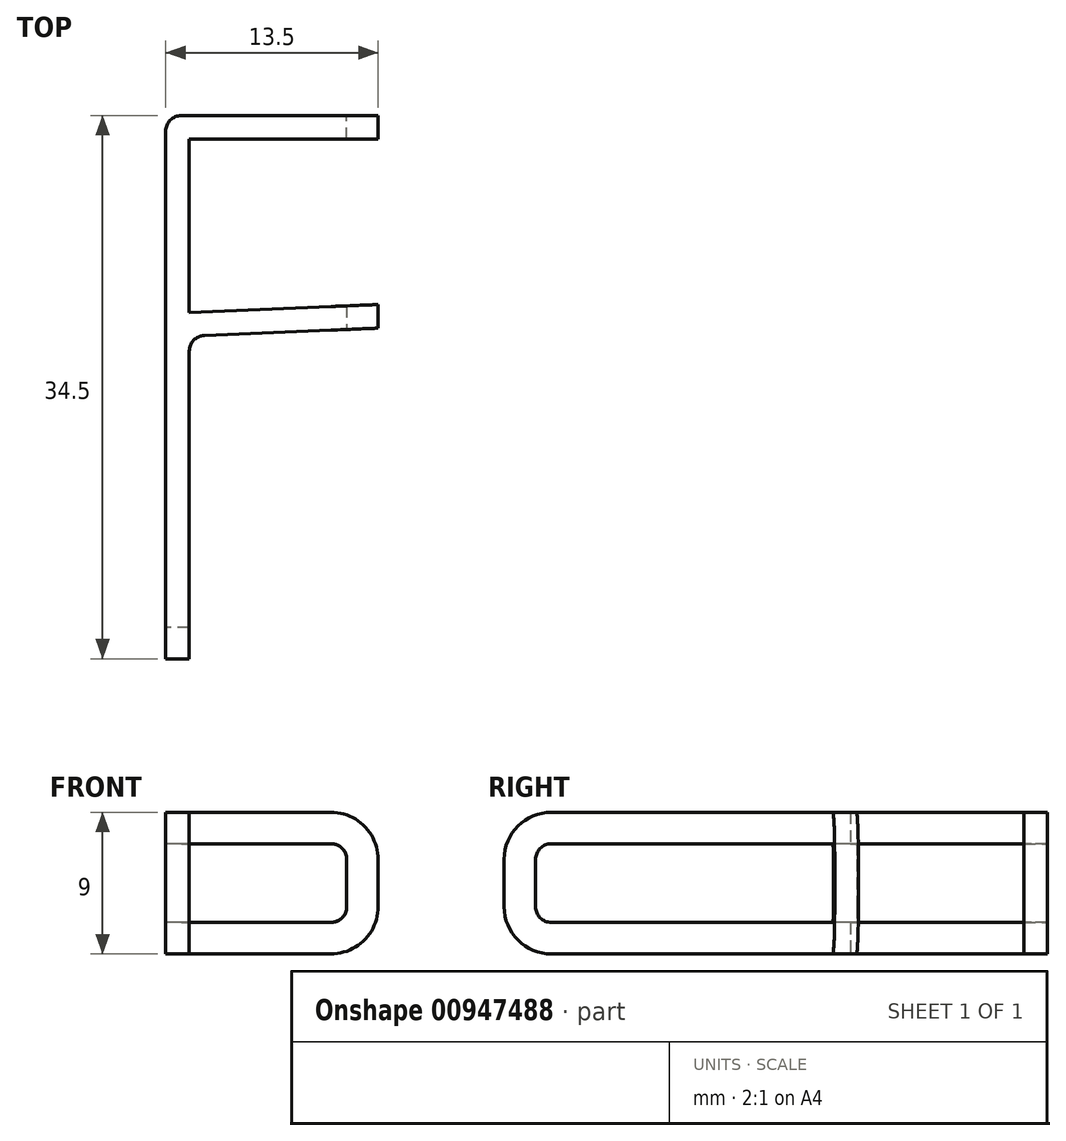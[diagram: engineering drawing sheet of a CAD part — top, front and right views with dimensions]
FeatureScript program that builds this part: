
annotation { "Feature Type Name" : "Feature", "Feature Type Description" : "" }
export const myFeature = defineFeature(function(context is Context, id is Id, definition is map)
    precondition{}
    {
        {
            var Q0;
            Q0=qCreatedBy(makeId("Top.planeOp"),FACE);
            var sketch = newSketch(context, id + "F0", { "sketchPlane" : qUnion([Q0])});
            skLineSegment(sketch, "E0", {"start": v(-63.6, 10) * mm, "end": v(-2.42, 20) * mm});
            skLineSegment(sketch, "E1", {"start": v(-2.42, 20) * mm, "end": v(-5.69, 40) * mm});
            skLineSegment(sketch, "E2", {"start": v(4.45, 40) * mm, "end": v(10.98, 0) * mm});
            skLineSegment(sketch, "E3", {"start": v(-0.76, 9.84) * mm, "end": v(0.85, 0) * mm});
            skLineSegment(sketch, "E4", {"start": v(0.85, 0) * mm, "end": v(10.98, 0) * mm});
            skLineSegment(sketch, "E5", {"start": v(-72.1, 0) * mm, "end": v(-63.6, 0) * mm});
            skLineSegment(sketch, "E6", {"start": v(-63.6, 0) * mm, "end": v(-0.76, 9.84) * mm});
            skLineSegment(sketch, "E7", {"start": v(-132.1, 0) * mm, "end": v(-120.08, 0) * mm});
            skLineSegment(sketch, "E8", {"start": v(-81.15, 53.94) * mm, "end": v(-72.1, 0) * mm});
            skLineSegment(sketch, "E9.trimOffspring", {"start": v(-71.34, 55.53) * mm, "end": v(-63.6, 10) * mm});
            skLineSegment(sketch, "E10", {"start": v(-73.25, 67.21) * mm, "end": v(-71.34, 55.53) * mm});
            skLineSegment(sketch, "E11", {"start": v(-87.24, 67.21) * mm, "end": v(-132.1, 0) * mm});
            skLineSegment(sketch, "E12.0", {"start": v(-81.74, 57.44) * mm, "end": v(-120.08, 0) * mm});
            skLineSegment(sketch, "E13", {"start": v(-72.1, 0) * mm, "end": v(-81.74, 57.44) * mm});
            skLineSegment(sketch, "E14", {"start": v(-87.24, 67.21) * mm, "end": v(-73.25, 67.21) * mm});
            skLineSegment(sketch, "E15", {"start": v(-2.42, 20) * mm, "end": v(2.58, 20) * mm});
            skLineSegment(sketch, "E16.0", {"start": v(-5.69, 40) * mm, "end": v(4.45, 40) * mm});
            skSolve(sketch);
        }
        {
            var Q0;
            Q0=makeQuery(id+"F0.imprint","IMPRINT",FACE,{"disambiguationData":[TD([[makeQuery(id+"F0.imprint","IMPRINT",EDGE,{"derivedFrom":sQuery(id+"F0.wireOp",EDGE,"E0")}),-1.0]])]});
            extrude(context, id + "F1", {"entities" : qUnion([Q0]), "depth" : 2.5 * mm, "offsetDistance" : 25 * mm, "hasSecondDirection" : true, "secondDirectionOppositeDirection" : true, "secondDirectionDepth" : 2.5 * mm});
        }
        {
            var Q0;
            Q0=makeQuery(id+"F1.opExtrude","CAP_EDGE",EDGE,{"disambiguationData":[OSD([sQuery(id+"F0.wireOp",EDGE,"E14")])],"isStart":false});
            chamfer(context, id + "F2", {"entities" : qUnion([Q0]), "chamferType" : ChamferType.TWO_OFFSETS, "width1" : 2 * mm, "oppositeDirection" : false, "width2" : 1 * mm, "tangentPropagation" : true});
        }
        {
            var Q0;
            {var subQ0=sQuery(id+"F0.wireOp",EDGE,"E14");Q0=makeQuery(id+"F2.opChamfer","BLEND_EDGE",EDGE,{"blendedFrom":[makeQuery(id+"F1.opExtrude","CAP_EDGE",EDGE,{"disambiguationData":[OSD([subQ0])],"isStart":false}),makeQuery(id+"F1.opExtrude","CAP_FACE",FACE,{"disambiguationData":[OSD([sQuery(id+"F0.wireOp",EDGE,"E0"),sQuery(id+"F0.wireOp",EDGE,"E1"),sQuery(id+"F0.wireOp",EDGE,"E2"),sQuery(id+"F0.wireOp",EDGE,"E3"),sQuery(id+"F0.wireOp",EDGE,"E4"),sQuery(id+"F0.wireOp",EDGE,"E5"),sQuery(id+"F0.wireOp",EDGE,"E6"),sQuery(id+"F0.wireOp",EDGE,"E7"),sQuery(id+"F0.wireOp",EDGE,"E9.trimOffspring"),sQuery(id+"F0.wireOp",EDGE,"E10"),sQuery(id+"F0.wireOp",EDGE,"E11"),sQuery(id+"F0.wireOp",EDGE,"E12.0"),sQuery(id+"F0.wireOp",EDGE,"E13"),subQ0,sQuery(id+"F0.wireOp",EDGE,"hnBKrzcR-41PN-ag7l-61eP-cGCsyuhvVwYe")])],"isStart":false})],"blendedInto":[makeQuery(id+"F1.opExtrude","CAP_FACE",FACE,{"disambiguationData":[OSD([sQuery(id+"F0.wireOp",EDGE,"E0"),sQuery(id+"F0.wireOp",EDGE,"E1"),sQuery(id+"F0.wireOp",EDGE,"E2"),sQuery(id+"F0.wireOp",EDGE,"E3"),sQuery(id+"F0.wireOp",EDGE,"E4"),sQuery(id+"F0.wireOp",EDGE,"E5"),sQuery(id+"F0.wireOp",EDGE,"E6"),sQuery(id+"F0.wireOp",EDGE,"E7"),sQuery(id+"F0.wireOp",EDGE,"E9.trimOffspring"),sQuery(id+"F0.wireOp",EDGE,"E10"),sQuery(id+"F0.wireOp",EDGE,"E11"),sQuery(id+"F0.wireOp",EDGE,"E12.0"),sQuery(id+"F0.wireOp",EDGE,"E13"),subQ0,sQuery(id+"F0.wireOp",EDGE,"hnBKrzcR-41PN-ag7l-61eP-cGCsyuhvVwYe")])],"isStart":false})]});}
            fillet(context, id + "F3", {"entities" : qUnion([Q0]), "radius" : 3 * mm, "tangentPropagation" : true, "allowEdgeOverflow" : false});
        }
        {
            var Q0;
            Q0=makeQuery(id+"F0.imprint","IMPRINT",FACE,{"disambiguationData":[TD([[makeQuery(id+"F0.imprint","IMPRINT",EDGE,{"derivedFrom":sQuery(id+"F0.wireOp",EDGE,"E0")}),-1.0]])]});
            extrude(context, id + "F4", {"entities" : qUnion([Q0]), "depth" : 9 * mm, "offsetDistance" : 25 * mm, "hasSecondDirection" : true, "secondDirectionOppositeDirection" : false, "secondDirectionDepth" : 4 * mm});
        }
        {
            var Q0;
            Q0=makeQuery(id+"F4.opExtrude","SWEPT_EDGE",EDGE,{"disambiguationData":[OSD([sQuery(id+"F0.wireOp",EDGE,"E12.0"),sQuery(id+"F0.wireOp",EDGE,"E13")])]});
            var Q1;
            Q1=makeQuery(id+"F1.opExtrude","SWEPT_EDGE",EDGE,{"disambiguationData":[OSD([sQuery(id+"F0.wireOp",EDGE,"E12.0"),sQuery(id+"F0.wireOp",EDGE,"E13")])]});
            var Q2;
            Q2=makeQuery(id+"F4.opExtrude","SWEPT_EDGE",EDGE,{"disambiguationData":[OSD([sQuery(id+"F0.wireOp",EDGE,"E5"),sQuery(id+"F0.wireOp",EDGE,"E13")])]});
            var Q3;
            Q3=makeQuery(id+"F1.opExtrude","SWEPT_EDGE",EDGE,{"disambiguationData":[OSD([sQuery(id+"F0.wireOp",EDGE,"E5"),sQuery(id+"F0.wireOp",EDGE,"E13")])]});
            var Q4;
            Q4=makeQuery(id+"F4.opExtrude","SWEPT_EDGE",EDGE,{"disambiguationData":[OSD([sQuery(id+"F0.wireOp",EDGE,"E7"),sQuery(id+"F0.wireOp",EDGE,"E12.0")])]});
            var Q5;
            Q5=makeQuery(id+"F1.opExtrude","SWEPT_EDGE",EDGE,{"disambiguationData":[OSD([sQuery(id+"F0.wireOp",EDGE,"E7"),sQuery(id+"F0.wireOp",EDGE,"E12.0")])]});
            var Q6;
            Q6=makeQuery(id+"F4.opExtrude","SWEPT_EDGE",EDGE,{"disambiguationData":[OSD([sQuery(id+"F0.wireOp",EDGE,"E3"),sQuery(id+"F0.wireOp",EDGE,"E4")])]});
            var Q7;
            Q7=makeQuery(id+"F1.opExtrude","SWEPT_EDGE",EDGE,{"disambiguationData":[OSD([sQuery(id+"F0.wireOp",EDGE,"E3"),sQuery(id+"F0.wireOp",EDGE,"E4")])]});
            var Q8;
            Q8=makeQuery(id+"F4.opExtrude","SWEPT_EDGE",EDGE,{"disambiguationData":[OSD([sQuery(id+"F0.wireOp",EDGE,"E11"),sQuery(id+"F0.wireOp",EDGE,"E14")])]});
            var Q9;
            Q9=makeQuery(id+"F1.opExtrude","SWEPT_EDGE",EDGE,{"disambiguationData":[OSD([sQuery(id+"F0.wireOp",EDGE,"E11"),sQuery(id+"F0.wireOp",EDGE,"E14")])]});
            var Q10;
            Q10=makeQuery(id+"F4.opExtrude","SWEPT_EDGE",EDGE,{"disambiguationData":[OSD([sQuery(id+"F0.wireOp",EDGE,"E10"),sQuery(id+"F0.wireOp",EDGE,"E14")])]});
            var Q11;
            Q11=makeQuery(id+"F1.opExtrude","SWEPT_EDGE",EDGE,{"disambiguationData":[OSD([sQuery(id+"F0.wireOp",EDGE,"E10"),sQuery(id+"F0.wireOp",EDGE,"E14")])]});
            var Q12;
            Q12=makeQuery(id+"F4.opExtrude","SWEPT_EDGE",EDGE,{"disambiguationData":[OSD([sQuery(id+"F0.wireOp",EDGE,"E2"),sQuery(id+"F0.wireOp",EDGE,"E16.0")])]});
            var Q13;
            Q13=makeQuery(id+"F1.opExtrude","SWEPT_EDGE",EDGE,{"disambiguationData":[OSD([sQuery(id+"F0.wireOp",EDGE,"E2"),sQuery(id+"F0.wireOp",EDGE,"E16.0")])]});
            fillet(context, id + "F5", {"entities" : qUnion([Q0, Q1, Q2, Q3, Q4, Q5, Q6, Q7, Q8, Q9, Q10, Q11, Q12, Q13]), "radius" : 5 * mm, "tangentPropagation" : true, "allowEdgeOverflow" : false});
        }
        {
            var Q0;
            Q0=makeQuery(id+"F1.opExtrude","SWEPT_EDGE",EDGE,{"disambiguationData":[OSD([sQuery(id+"F0.wireOp",EDGE,"E0"),sQuery(id+"F0.wireOp",EDGE,"E1")])]});
            var Q1;
            Q1=makeQuery(id+"F4.opExtrude","SWEPT_EDGE",EDGE,{"disambiguationData":[OSD([sQuery(id+"F0.wireOp",EDGE,"E0"),sQuery(id+"F0.wireOp",EDGE,"E1")])]});
            var Q2;
            Q2=makeQuery(id+"F4.opExtrude","SWEPT_EDGE",EDGE,{"disambiguationData":[OSD([sQuery(id+"F0.wireOp",EDGE,"E0"),sQuery(id+"F0.wireOp",EDGE,"E9.trimOffspring")])]});
            var Q3;
            Q3=makeQuery(id+"F1.opExtrude","SWEPT_EDGE",EDGE,{"disambiguationData":[OSD([sQuery(id+"F0.wireOp",EDGE,"E0"),sQuery(id+"F0.wireOp",EDGE,"E9.trimOffspring")])]});
            var Q4;
            Q4=makeQuery(id+"F1.opExtrude","SWEPT_EDGE",EDGE,{"disambiguationData":[OSD([sQuery(id+"F0.wireOp",EDGE,"E3"),sQuery(id+"F0.wireOp",EDGE,"E6")])]});
            var Q5;
            Q5=makeQuery(id+"F4.opExtrude","SWEPT_EDGE",EDGE,{"disambiguationData":[OSD([sQuery(id+"F0.wireOp",EDGE,"E3"),sQuery(id+"F0.wireOp",EDGE,"E6")])]});
            var Q6;
            Q6=makeQuery(id+"F1.opExtrude","SWEPT_EDGE",EDGE,{"disambiguationData":[OSD([sQuery(id+"F0.wireOp",EDGE,"E1"),sQuery(id+"F0.wireOp",EDGE,"hnBKrzcR-41PN-ag7l-61eP-cGCsyuhvVwYe")])]});
            var Q7;
            Q7=makeQuery(id+"F4.opExtrude","SWEPT_EDGE",EDGE,{"disambiguationData":[OSD([sQuery(id+"F0.wireOp",EDGE,"E1"),sQuery(id+"F0.wireOp",EDGE,"hnBKrzcR-41PN-ag7l-61eP-cGCsyuhvVwYe")])]});
            var Q8;
            Q8=makeQuery(id+"F4.opExtrude","SWEPT_EDGE",EDGE,{"disambiguationData":[OSD([sQuery(id+"F0.wireOp",EDGE,"E2"),sQuery(id+"F0.wireOp",EDGE,"E4")])]});
            var Q9;
            Q9=makeQuery(id+"F1.opExtrude","SWEPT_EDGE",EDGE,{"disambiguationData":[OSD([sQuery(id+"F0.wireOp",EDGE,"E2"),sQuery(id+"F0.wireOp",EDGE,"E4")])]});
            var Q10;
            Q10=makeQuery(id+"F1.opExtrude","SWEPT_EDGE",EDGE,{"disambiguationData":[OSD([sQuery(id+"F0.wireOp",EDGE,"E7"),sQuery(id+"F0.wireOp",EDGE,"E11")])]});
            var Q11;
            Q11=makeQuery(id+"F4.opExtrude","SWEPT_EDGE",EDGE,{"disambiguationData":[OSD([sQuery(id+"F0.wireOp",EDGE,"E7"),sQuery(id+"F0.wireOp",EDGE,"E11")])]});
            fillet(context, id + "F6", {"entities" : qUnion([Q0, Q1, Q2, Q3, Q4, Q5, Q6, Q7, Q8, Q9, Q10, Q11]), "radius" : 2 * mm, "tangentPropagation" : true, "allowEdgeOverflow" : false});
        }
        {
            var Q0;
            Q0=qCreatedBy(makeId("Top.planeOp"),FACE);
            var sketch = newSketch(context, id + "F7", { "sketchPlane" : qUnion([Q0])});
            skLineSegment(sketch, "E17", {"start": v(-79.91, 59.99) * mm, "end": v(-79.91, 60.49) * mm});
            skLineSegment(sketch, "E18", {"start": v(-79.91, 60.49) * mm, "end": v(-79.91, 65.49) * mm});
            skLineSegment(sketch, "E19", {"start": v(-79.91, 65.49) * mm, "end": v(-82.41, 65.49) * mm});
            skLineSegment(sketch, "E20", {"start": v(-79.91, 65.49) * mm, "end": v(-77.41, 65.49) * mm});
            skLineSegment(sketch, "E21", {"start": v(-77.41, 65.49) * mm, "end": v(-77.41, 60.49) * mm});
            skLineSegment(sketch, "E22", {"start": v(-77.41, 60.49) * mm, "end": v(-79.91, 60.49) * mm});
            skLineSegment(sketch, "E23", {"start": v(-79.91, 60.49) * mm, "end": v(-82.41, 60.49) * mm});
            skLineSegment(sketch, "E24", {"start": v(-82.41, 60.49) * mm, "end": v(-82.41, 65.49) * mm});
            skLineSegment(sketch, "E25.0", {"start": v(-79.91, 65.99) * mm, "end": v(-76.91, 65.99) * mm});
            skLineSegment(sketch, "E25.1", {"start": v(-82.91, 59.99) * mm, "end": v(-82.91, 65.99) * mm});
            skLineSegment(sketch, "E25.2", {"start": v(-79.91, 59.99) * mm, "end": v(-82.91, 59.99) * mm});
            skLineSegment(sketch, "E25.3", {"start": v(-79.91, 65.99) * mm, "end": v(-82.91, 65.99) * mm});
            skLineSegment(sketch, "E25.4", {"start": v(-76.91, 59.99) * mm, "end": v(-79.91, 59.99) * mm});
            skLineSegment(sketch, "E25.5", {"start": v(-76.91, 65.99) * mm, "end": v(-76.91, 59.99) * mm});
            skLineSegment(sketch, "E26", {"start": v(-82.41, 62.99) * mm, "end": v(-85.71, 62.99) * mm});
            skLineSegment(sketch, "E27", {"start": v(-85.71, 62.99) * mm, "end": v(-85.71, 63.49) * mm});
            skLineSegment(sketch, "E28", {"start": v(-85.71, 63.49) * mm, "end": v(-82.41, 65.49) * mm});
            skLineSegment(sketch, "E29.0", {"start": v(-86.21, 62.99) * mm, "end": v(-86.21, 63.49) * mm});
            skLineSegment(sketch, "E30", {"start": v(-86.21, 63.49) * mm, "end": v(-82.09, 65.99) * mm});
            skLineSegment(sketch, "E31", {"start": v(-86.21, 62.99) * mm, "end": v(-85.71, 62.99) * mm});
            skLineSegment(sketch, "E32", {"start": v(-82.41, 62.99) * mm, "end": v(-77.41, 62.99) * mm});
            skLineSegment(sketch, "E33.MirrorCS", {"start": v(-73.61, 63.49) * mm, "end": v(-77.74, 65.99) * mm});
            skLineSegment(sketch, "E34.MirrorCS", {"start": v(-74.11, 63.49) * mm, "end": v(-77.41, 65.49) * mm});
            skLineSegment(sketch, "E35.MirrorCS", {"start": v(-73.61, 62.99) * mm, "end": v(-73.61, 63.49) * mm});
            skLineSegment(sketch, "E36.MirrorCS", {"start": v(-74.11, 62.99) * mm, "end": v(-74.11, 63.49) * mm});
            skLineSegment(sketch, "E37.MirrorCS", {"start": v(-73.61, 62.99) * mm, "end": v(-74.11, 62.99) * mm});
            skLineSegment(sketch, "E38.MirrorCS", {"start": v(-77.41, 62.99) * mm, "end": v(-74.11, 62.99) * mm});
            skLineSegment(sketch, "E39", {"start": v(-82.91, 65.99) * mm, "end": v(-82.91, 68.99) * mm});
            skLineSegment(sketch, "E40", {"start": v(-82.91, 68.99) * mm, "end": v(-76.91, 68.99) * mm});
            skLineSegment(sketch, "E41", {"start": v(-76.91, 68.99) * mm, "end": v(-76.91, 65.99) * mm});
            skSolve(sketch);
        }
        {
            var Q0;
            {var subQ0=sQuery(id+"F7.wireOp",EDGE,"E39");Q0=makeQuery(id+"F7.imprint","IMPRINT",FACE,{"disambiguationData":[TD([[makeQuery(id+"F7.imprint","IMPRINT",EDGE,{"derivedFrom":subQ0}),-1.0]])]});}
            var Q1;
            {var subQ15=sQuery(id+"F7.wireOp",EDGE,"E19");Q1=makeQuery(id+"F7.imprint","IMPRINT",FACE,{"disambiguationData":[TD([[makeQuery(id+"F7.imprint","IMPRINT",EDGE,{"derivedFrom":subQ15}),-1.0]])]});}
            var Q2;
            {var subQ0=sQuery(id+"F7.wireOp",EDGE,"E25.3");var subQ3=sQuery(id+"F7.wireOp",EDGE,"E30");var subQ5=makeQuery(id+"F7.imprint","INTERSECT",VERTEX,{"derivedFrom":[subQ0,subQ3]});Q2=makeQuery(id+"F7.imprint","IMPRINT",FACE,{"disambiguationData":[TD([[makeQuery(id+"F7.imprint","IMPRINT",EDGE,{"disambiguationData":[TD([[subQ5,1.0]])],"derivedFrom":subQ3}),1.0]])]});}
            var Q3;
            {var subQ1=sQuery(id+"F7.wireOp",EDGE,"E25.0");var subQ3=sQuery(id+"F7.wireOp",EDGE,"E33.MirrorCS");var subQ4=makeQuery(id+"F7.imprint","INTERSECT",VERTEX,{"derivedFrom":[subQ1,subQ3]});Q3=makeQuery(id+"F7.imprint","IMPRINT",FACE,{"disambiguationData":[TD([[makeQuery(id+"F7.imprint","IMPRINT",EDGE,{"disambiguationData":[TD([[subQ4,1.0]])],"derivedFrom":subQ3}),-1.0]])]});}
            var Q4;
            {var subQ3=sQuery(id+"F7.wireOp",EDGE,"E26");var subQ5=sQuery(id+"F7.wireOp",EDGE,"E25.1");var subQ6=makeQuery(id+"F7.imprint","INTERSECT",VERTEX,{"derivedFrom":[subQ5,subQ3]});Q4=makeQuery(id+"F7.imprint","IMPRINT",FACE,{"disambiguationData":[TD([[makeQuery(id+"F7.imprint","IMPRINT",EDGE,{"disambiguationData":[TD([[subQ6,-1.0]])],"derivedFrom":subQ5}),-1.0]])]});}
            var Q5;
            {var subQ0=sQuery(id+"F7.wireOp",EDGE,"E19");Q5=makeQuery(id+"F7.imprint","IMPRINT",FACE,{"disambiguationData":[TD([[makeQuery(id+"F7.imprint","IMPRINT",EDGE,{"derivedFrom":subQ0}),1.0]])]});}
            var Q6;
            {var subQ0=sQuery(id+"F7.wireOp",EDGE,"E20");Q6=makeQuery(id+"F7.imprint","IMPRINT",FACE,{"disambiguationData":[TD([[makeQuery(id+"F7.imprint","IMPRINT",EDGE,{"derivedFrom":subQ0}),-1.0]])]});}
            var Q7;
            {var subQ3=sQuery(id+"F7.wireOp",EDGE,"E38.MirrorCS");var subQ5=sQuery(id+"F7.wireOp",EDGE,"E25.5");var subQ6=makeQuery(id+"F7.imprint","INTERSECT",VERTEX,{"derivedFrom":[subQ5,subQ3]});Q7=makeQuery(id+"F7.imprint","IMPRINT",FACE,{"disambiguationData":[TD([[makeQuery(id+"F7.imprint","IMPRINT",EDGE,{"disambiguationData":[TD([[subQ6,1.0]])],"derivedFrom":subQ5}),-1.0]])]});}
            var Q8;
            Q8=sQuery(id+"F7.wireOp",EDGE,"E32");
            revolve(context, id + "F8", {"operationType" : NewBodyOperationType.REMOVE, "surfaceOperationType" : NewSurfaceOperationType.NEW, "entities" : qUnion([Q0, Q1, Q2, Q3, Q4, Q5, Q6, Q7]), "axis" : qUnion([Q8]), "revolveType" : RevolveType.ONE_DIRECTION, "oppositeDirection" : true, "angle" : 90 * degree});
        }
        {
            var Q0;
            {var subQ0=sQuery(id+"F7.wireOp",EDGE,"E39");Q0=makeQuery(id+"F7.imprint","IMPRINT",FACE,{"disambiguationData":[TD([[makeQuery(id+"F7.imprint","IMPRINT",EDGE,{"derivedFrom":subQ0}),-1.0]])]});}
            var Q1;
            {var subQ0=sQuery(id+"F7.wireOp",EDGE,"E25.3");var subQ3=sQuery(id+"F7.wireOp",EDGE,"E30");var subQ5=makeQuery(id+"F7.imprint","INTERSECT",VERTEX,{"derivedFrom":[subQ0,subQ3]});Q1=makeQuery(id+"F7.imprint","IMPRINT",FACE,{"disambiguationData":[TD([[makeQuery(id+"F7.imprint","IMPRINT",EDGE,{"disambiguationData":[TD([[subQ5,1.0]])],"derivedFrom":subQ3}),1.0]])]});}
            var Q2;
            {var subQ1=sQuery(id+"F7.wireOp",EDGE,"E25.0");var subQ3=sQuery(id+"F7.wireOp",EDGE,"E33.MirrorCS");var subQ4=makeQuery(id+"F7.imprint","INTERSECT",VERTEX,{"derivedFrom":[subQ1,subQ3]});Q2=makeQuery(id+"F7.imprint","IMPRINT",FACE,{"disambiguationData":[TD([[makeQuery(id+"F7.imprint","IMPRINT",EDGE,{"disambiguationData":[TD([[subQ4,1.0]])],"derivedFrom":subQ3}),-1.0]])]});}
            var Q3;
            {var subQ15=sQuery(id+"F7.wireOp",EDGE,"E19");Q3=makeQuery(id+"F7.imprint","IMPRINT",FACE,{"disambiguationData":[TD([[makeQuery(id+"F7.imprint","IMPRINT",EDGE,{"derivedFrom":subQ15}),-1.0]])]});}
            var Q4;
            {var subQ3=sQuery(id+"F7.wireOp",EDGE,"E26");var subQ5=sQuery(id+"F7.wireOp",EDGE,"E25.1");var subQ6=makeQuery(id+"F7.imprint","INTERSECT",VERTEX,{"derivedFrom":[subQ5,subQ3]});Q4=makeQuery(id+"F7.imprint","IMPRINT",FACE,{"disambiguationData":[TD([[makeQuery(id+"F7.imprint","IMPRINT",EDGE,{"disambiguationData":[TD([[subQ6,-1.0]])],"derivedFrom":subQ5}),-1.0]])]});}
            var Q5;
            {var subQ0=sQuery(id+"F7.wireOp",EDGE,"E19");Q5=makeQuery(id+"F7.imprint","IMPRINT",FACE,{"disambiguationData":[TD([[makeQuery(id+"F7.imprint","IMPRINT",EDGE,{"derivedFrom":subQ0}),1.0]])]});}
            var Q6;
            {var subQ0=sQuery(id+"F7.wireOp",EDGE,"E20");Q6=makeQuery(id+"F7.imprint","IMPRINT",FACE,{"disambiguationData":[TD([[makeQuery(id+"F7.imprint","IMPRINT",EDGE,{"derivedFrom":subQ0}),-1.0]])]});}
            var Q7;
            {var subQ3=sQuery(id+"F7.wireOp",EDGE,"E38.MirrorCS");var subQ5=sQuery(id+"F7.wireOp",EDGE,"E25.5");var subQ6=makeQuery(id+"F7.imprint","INTERSECT",VERTEX,{"derivedFrom":[subQ5,subQ3]});Q7=makeQuery(id+"F7.imprint","IMPRINT",FACE,{"disambiguationData":[TD([[makeQuery(id+"F7.imprint","IMPRINT",EDGE,{"disambiguationData":[TD([[subQ6,1.0]])],"derivedFrom":subQ5}),-1.0]])]});}
            var Q8;
            Q8=makeQuery(id+"F7.imprint","IMPRINT",FACE,{"disambiguationData":[TD([[makeQuery(id+"F7.imprint","IMPRINT",EDGE,{"derivedFrom":sQuery(id+"F7.wireOp",EDGE,"E17")}),1.0]])]});
            var Q9;
            {var subQ0=sQuery(id+"F7.wireOp",EDGE,"E23");Q9=makeQuery(id+"F7.imprint","IMPRINT",FACE,{"disambiguationData":[TD([[makeQuery(id+"F7.imprint","IMPRINT",EDGE,{"derivedFrom":subQ0}),-1.0]])]});}
            var Q10;
            {var subQ0=sQuery(id+"F7.wireOp",EDGE,"E22");Q10=makeQuery(id+"F7.imprint","IMPRINT",FACE,{"disambiguationData":[TD([[makeQuery(id+"F7.imprint","IMPRINT",EDGE,{"derivedFrom":subQ0}),-1.0]])]});}
            var Q11;
            Q11=makeQuery(id+"F7.imprint","IMPRINT",FACE,{"disambiguationData":[TD([[makeQuery(id+"F7.imprint","IMPRINT",EDGE,{"derivedFrom":sQuery(id+"F7.wireOp",EDGE,"E17")}),-1.0]])]});
            extrude(context, id + "F9", {"entities" : qUnion([Q0, Q1, Q2, Q3, Q4, Q5, Q6, Q7, Q8, Q9, Q10, Q11]), "operationType" : NewBodyOperationType.REMOVE, "depth" : 10 * mm, "offsetDistance" : 25 * mm});
        }
        {
            var Q0;
            {var subQ1=sQuery(id+"F7.wireOp",EDGE,"E27");Q0=makeQuery(id+"F7.imprint","IMPRINT",FACE,{"disambiguationData":[TD([[makeQuery(id+"F7.imprint","IMPRINT",EDGE,{"derivedFrom":subQ1}),1.0]])]});}
            var Q1;
            {var subQ5=sQuery(id+"F7.wireOp",EDGE,"E27");Q1=makeQuery(id+"F7.imprint","IMPRINT",FACE,{"disambiguationData":[TD([[makeQuery(id+"F7.imprint","IMPRINT",EDGE,{"derivedFrom":subQ5}),-1.0]])]});}
            var Q2;
            {var subQ15=sQuery(id+"F7.wireOp",EDGE,"E19");Q2=makeQuery(id+"F7.imprint","IMPRINT",FACE,{"disambiguationData":[TD([[makeQuery(id+"F7.imprint","IMPRINT",EDGE,{"derivedFrom":subQ15}),-1.0]])]});}
            var Q3;
            {var subQ3=sQuery(id+"F7.wireOp",EDGE,"E26");var subQ5=sQuery(id+"F7.wireOp",EDGE,"E25.1");var subQ6=makeQuery(id+"F7.imprint","INTERSECT",VERTEX,{"derivedFrom":[subQ5,subQ3]});Q3=makeQuery(id+"F7.imprint","IMPRINT",FACE,{"disambiguationData":[TD([[makeQuery(id+"F7.imprint","IMPRINT",EDGE,{"disambiguationData":[TD([[subQ6,-1.0]])],"derivedFrom":subQ5}),-1.0]])]});}
            var Q4;
            {var subQ0=sQuery(id+"F7.wireOp",EDGE,"E19");Q4=makeQuery(id+"F7.imprint","IMPRINT",FACE,{"disambiguationData":[TD([[makeQuery(id+"F7.imprint","IMPRINT",EDGE,{"derivedFrom":subQ0}),1.0]])]});}
            var Q5;
            {var subQ0=sQuery(id+"F7.wireOp",EDGE,"E20");Q5=makeQuery(id+"F7.imprint","IMPRINT",FACE,{"disambiguationData":[TD([[makeQuery(id+"F7.imprint","IMPRINT",EDGE,{"derivedFrom":subQ0}),-1.0]])]});}
            var Q6;
            {var subQ3=sQuery(id+"F7.wireOp",EDGE,"E38.MirrorCS");var subQ5=sQuery(id+"F7.wireOp",EDGE,"E25.5");var subQ6=makeQuery(id+"F7.imprint","INTERSECT",VERTEX,{"derivedFrom":[subQ5,subQ3]});Q6=makeQuery(id+"F7.imprint","IMPRINT",FACE,{"disambiguationData":[TD([[makeQuery(id+"F7.imprint","IMPRINT",EDGE,{"disambiguationData":[TD([[subQ6,1.0]])],"derivedFrom":subQ5}),-1.0]])]});}
            var Q7;
            {var subQ5=sQuery(id+"F7.wireOp",EDGE,"E36.MirrorCS");Q7=makeQuery(id+"F7.imprint","IMPRINT",FACE,{"disambiguationData":[TD([[makeQuery(id+"F7.imprint","IMPRINT",EDGE,{"derivedFrom":subQ5}),1.0]])]});}
            var Q8;
            {var subQ0=sQuery(id+"F7.wireOp",EDGE,"E35.MirrorCS");Q8=makeQuery(id+"F7.imprint","IMPRINT",FACE,{"disambiguationData":[TD([[makeQuery(id+"F7.imprint","IMPRINT",EDGE,{"derivedFrom":subQ0}),1.0]])]});}
            var Q9;
            Q9=sQuery(id+"F7.wireOp",EDGE,"E38.MirrorCS");
            revolve(context, id + "F10", {"operationType" : NewBodyOperationType.REMOVE, "surfaceOperationType" : NewSurfaceOperationType.NEW, "entities" : qUnion([Q0, Q1, Q2, Q3, Q4, Q5, Q6, Q7, Q8]), "axis" : qUnion([Q9]), "revolveType" : RevolveType.FULL});
        }
        {
            var Q0;
            {var subQ0=sQuery(id+"F7.wireOp",EDGE,"E20");Q0=makeQuery(id+"F7.imprint","IMPRINT",FACE,{"disambiguationData":[TD([[makeQuery(id+"F7.imprint","IMPRINT",EDGE,{"derivedFrom":subQ0}),-1.0]])]});}
            var Q1;
            {var subQ0=sQuery(id+"F7.wireOp",EDGE,"E19");Q1=makeQuery(id+"F7.imprint","IMPRINT",FACE,{"disambiguationData":[TD([[makeQuery(id+"F7.imprint","IMPRINT",EDGE,{"derivedFrom":subQ0}),1.0]])]});}
            var Q2;
            {var subQ0=sQuery(id+"F7.wireOp",EDGE,"E22");Q2=makeQuery(id+"F7.imprint","IMPRINT",FACE,{"disambiguationData":[TD([[makeQuery(id+"F7.imprint","IMPRINT",EDGE,{"derivedFrom":subQ0}),-1.0]])]});}
            var Q3;
            {var subQ0=sQuery(id+"F7.wireOp",EDGE,"E23");Q3=makeQuery(id+"F7.imprint","IMPRINT",FACE,{"disambiguationData":[TD([[makeQuery(id+"F7.imprint","IMPRINT",EDGE,{"derivedFrom":subQ0}),-1.0]])]});}
            extrude(context, id + "F11", {"entities" : qUnion([Q0, Q1, Q2, Q3]), "operationType" : NewBodyOperationType.REMOVE, "depth" : 8 * mm, "offsetDistance" : 25 * mm});
        }
        {
            var Q0;
            {var subQ0=sQuery(id+"F7.wireOp",EDGE,"E19");Q0=makeQuery(id+"F7.imprint","IMPRINT",FACE,{"disambiguationData":[TD([[makeQuery(id+"F7.imprint","IMPRINT",EDGE,{"derivedFrom":subQ0}),1.0]])]});}
            var Q1;
            {var subQ0=sQuery(id+"F7.wireOp",EDGE,"E20");Q1=makeQuery(id+"F7.imprint","IMPRINT",FACE,{"disambiguationData":[TD([[makeQuery(id+"F7.imprint","IMPRINT",EDGE,{"derivedFrom":subQ0}),-1.0]])]});}
            var Q2;
            {var subQ0=sQuery(id+"F7.wireOp",EDGE,"E23");Q2=makeQuery(id+"F7.imprint","IMPRINT",FACE,{"disambiguationData":[TD([[makeQuery(id+"F7.imprint","IMPRINT",EDGE,{"derivedFrom":subQ0}),-1.0]])]});}
            var Q3;
            {var subQ0=sQuery(id+"F7.wireOp",EDGE,"E22");Q3=makeQuery(id+"F7.imprint","IMPRINT",FACE,{"disambiguationData":[TD([[makeQuery(id+"F7.imprint","IMPRINT",EDGE,{"derivedFrom":subQ0}),-1.0]])]});}
            extrude(context, id + "F12", {"entities" : qUnion([Q0, Q1, Q2, Q3]), "depth" : 8 * mm, "offsetDistance" : 25 * mm});
        }
        {
            var Q0;
            {var subQ5=sQuery(id+"F7.wireOp",EDGE,"E27");Q0=makeQuery(id+"F7.imprint","IMPRINT",FACE,{"disambiguationData":[TD([[makeQuery(id+"F7.imprint","IMPRINT",EDGE,{"derivedFrom":subQ5}),-1.0]])]});}
            var Q1;
            {var subQ3=sQuery(id+"F7.wireOp",EDGE,"E26");var subQ5=sQuery(id+"F7.wireOp",EDGE,"E25.1");var subQ6=makeQuery(id+"F7.imprint","INTERSECT",VERTEX,{"derivedFrom":[subQ5,subQ3]});Q1=makeQuery(id+"F7.imprint","IMPRINT",FACE,{"disambiguationData":[TD([[makeQuery(id+"F7.imprint","IMPRINT",EDGE,{"disambiguationData":[TD([[subQ6,-1.0]])],"derivedFrom":subQ5}),-1.0]])]});}
            var Q2;
            {var subQ0=sQuery(id+"F7.wireOp",EDGE,"E19");Q2=makeQuery(id+"F7.imprint","IMPRINT",FACE,{"disambiguationData":[TD([[makeQuery(id+"F7.imprint","IMPRINT",EDGE,{"derivedFrom":subQ0}),1.0]])]});}
            var Q3;
            {var subQ0=sQuery(id+"F7.wireOp",EDGE,"E20");Q3=makeQuery(id+"F7.imprint","IMPRINT",FACE,{"disambiguationData":[TD([[makeQuery(id+"F7.imprint","IMPRINT",EDGE,{"derivedFrom":subQ0}),-1.0]])]});}
            var Q4;
            {var subQ3=sQuery(id+"F7.wireOp",EDGE,"E38.MirrorCS");var subQ5=sQuery(id+"F7.wireOp",EDGE,"E25.5");var subQ6=makeQuery(id+"F7.imprint","INTERSECT",VERTEX,{"derivedFrom":[subQ5,subQ3]});Q4=makeQuery(id+"F7.imprint","IMPRINT",FACE,{"disambiguationData":[TD([[makeQuery(id+"F7.imprint","IMPRINT",EDGE,{"disambiguationData":[TD([[subQ6,1.0]])],"derivedFrom":subQ5}),-1.0]])]});}
            var Q5;
            {var subQ5=sQuery(id+"F7.wireOp",EDGE,"E36.MirrorCS");Q5=makeQuery(id+"F7.imprint","IMPRINT",FACE,{"disambiguationData":[TD([[makeQuery(id+"F7.imprint","IMPRINT",EDGE,{"derivedFrom":subQ5}),1.0]])]});}
            var Q6;
            Q6=sQuery(id+"F7.wireOp",EDGE,"E32");
            revolve(context, id + "F13", {"operationType" : NewBodyOperationType.ADD, "surfaceOperationType" : NewSurfaceOperationType.NEW, "entities" : qUnion([Q0, Q1, Q2, Q3, Q4, Q5]), "axis" : qUnion([Q6]), "revolveType" : RevolveType.FULL});
        }
        {
            var Q0;
            Q0=qCreatedBy(makeId("Top.planeOp"),FACE);
            var sketch = newSketch(context, id + "F14", { "sketchPlane" : qUnion([Q0])});
            skCircle(sketch, "E42", {"center": v(-81.45, 54.7) * mm, "radius": 2.5 * mm});
            skCircle(sketch, "E43", {"center": v(0.64, 35) * mm, "radius": 2.5 * mm});
            skCircle(sketch, "E44", {"center": v(5.1, 5) * mm, "radius": 2.5 * mm});
            skCircle(sketch, "E45", {"center": v(-67.87, 5) * mm, "radius": 2.5 * mm});
            skCircle(sketch, "E46", {"center": v(-122.75, 5) * mm, "radius": 2.5 * mm});
            skSolve(sketch);
        }
        {
            var Q0;
            Q0=makeQuery(id+"F14.imprint","IMPRINT",FACE,{"disambiguationData":[TD([[makeQuery(id+"F14.imprint","IMPRINT",EDGE,{"derivedFrom":sQuery(id+"F14.wireOp",EDGE,"E44")}),1.0]])]});
            var Q1;
            Q1=makeQuery(id+"F14.imprint","IMPRINT",FACE,{"disambiguationData":[TD([[makeQuery(id+"F14.imprint","IMPRINT",EDGE,{"derivedFrom":sQuery(id+"F14.wireOp",EDGE,"E43")}),1.0]])]});
            var Q2;
            Q2=makeQuery(id+"F14.imprint","IMPRINT",FACE,{"disambiguationData":[TD([[makeQuery(id+"F14.imprint","IMPRINT",EDGE,{"derivedFrom":sQuery(id+"F14.wireOp",EDGE,"E46")}),1.0]])]});
            var Q3;
            Q3=makeQuery(id+"F14.imprint","IMPRINT",FACE,{"disambiguationData":[TD([[makeQuery(id+"F14.imprint","IMPRINT",EDGE,{"derivedFrom":sQuery(id+"F14.wireOp",EDGE,"E45")}),1.0]])]});
            var Q4;
            Q4=makeQuery(id+"F14.imprint","IMPRINT",FACE,{"disambiguationData":[TD([[makeQuery(id+"F14.imprint","IMPRINT",EDGE,{"derivedFrom":sQuery(id+"F14.wireOp",EDGE,"E42")}),1.0]])]});
            extrude(context, id + "F15", {"entities" : qUnion([Q0, Q1, Q2, Q3, Q4]), "operationType" : NewBodyOperationType.ADD, "depth" : 4 * mm, "offsetDistance" : 25 * mm, "hasSecondDirection" : true, "secondDirectionOppositeDirection" : true, "secondDirectionDepth" : -2.5 * mm});
        }
        {
            var Q0;
            Q0=qCreatedBy(makeId("Top.planeOp"),FACE);
            var sketch = newSketch(context, id + "F16", { "sketchPlane" : qUnion([Q0])});
            skPoint(sketch, "E47", {"position": v(1.75, 23) * mm});
            skPoint(sketch, "E48", {"position": v(-79.9, 63) * mm});
            skLineSegment(sketch, "E49", {"start": v(-79.9, 63) * mm, "end": v(-110.43, 34.89) * mm});
            skLineSegment(sketch, "E50", {"start": v(-110.43, 34.89) * mm, "end": v(-47, 37.72) * mm});
            skLineSegment(sketch, "E51", {"start": v(-79.9, 63) * mm, "end": v(-47, 37.72) * mm});
            skLineSegment(sketch, "E52.bottom", {"start": v(-30.14, -0.3) * mm, "end": v(-18.14, -0.3) * mm});
            skLineSegment(sketch, "E52.top", {"start": v(-30.14, -11.3) * mm, "end": v(-18.14, -11.3) * mm});
            skLineSegment(sketch, "E52.left", {"start": v(-30.14, -0.3) * mm, "end": v(-30.14, -11.3) * mm});
            skLineSegment(sketch, "E53.0", {"start": v(-32.14, 1.7) * mm, "end": v(-18.14, 1.7) * mm});
            skLineSegment(sketch, "E53.1", {"start": v(-32.14, 1.7) * mm, "end": v(-32.14, -33.3) * mm});
            skLineSegment(sketch, "E53.2", {"start": v(-32.14, -13.3) * mm, "end": v(-18.14, -13.3) * mm});
            skLineSegment(sketch, "E54", {"start": v(-18.14, -0.3) * mm, "end": v(-18.14, 1.7) * mm});
            skLineSegment(sketch, "E55", {"start": v(-18.14, -11.3) * mm, "end": v(-18.14, -13.3) * mm});
            skLineSegment(sketch, "E56", {"start": v(-30.14, -11.3) * mm, "end": v(-30.14, -33.3) * mm});
            skLineSegment(sketch, "E57", {"start": v(-30.14, -33.3) * mm, "end": v(-32.14, -33.3) * mm});
            skLineSegment(sketch, "E58.bottom", {"start": v(1.47, -0.8) * mm, "end": v(13.47, -0.8) * mm});
            skLineSegment(sketch, "E58.left", {"start": v(1.47, -0.8) * mm, "end": v(1.47, -11.8) * mm});
            skLineSegment(sketch, "E59.0", {"start": v(-0.03, 0.7) * mm, "end": v(13.47, 0.7) * mm});
            skLineSegment(sketch, "E59.1", {"start": v(-0.03, 0.7) * mm, "end": v(-0.03, -33.8) * mm});
            skLineSegment(sketch, "E60", {"start": v(13.47, -0.8) * mm, "end": v(13.47, 0.7) * mm});
            skLineSegment(sketch, "E61", {"start": v(13.47, -11.8) * mm, "end": v(13.47, -12.8) * mm});
            skLineSegment(sketch, "E62", {"start": v(1.47, -11.8) * mm, "end": v(1.47, -33.8) * mm});
            skLineSegment(sketch, "E63", {"start": v(1.47, -33.8) * mm, "end": v(-0.03, -33.8) * mm});
            skLineSegment(sketch, "E64.0", {"start": v(11.47, -0.8) * mm, "end": v(11.47, 0.7) * mm});
            skLineSegment(sketch, "E65.0", {"start": v(11.47, -11.37) * mm, "end": v(11.47, -12.88) * mm});
            skLineSegment(sketch, "E66.0", {"start": v(1.47, -31.8) * mm, "end": v(-0.03, -31.8) * mm});
            skLineSegment(sketch, "E67", {"start": v(13.47, -11.8) * mm, "end": v(13.47, -11.3) * mm});
            skLineSegment(sketch, "E68", {"start": v(1.47, -11.8) * mm, "end": v(13.47, -11.3) * mm});
            skLineSegment(sketch, "E69.0", {"start": v(1.47, -13.3) * mm, "end": v(13.47, -12.8) * mm});
            skSolve(sketch);
        }
        {
            var Q0;
            Q0=makeQuery(id+"F16.imprint","IMPRINT",FACE,{"disambiguationData":[TD([[makeQuery(id+"F16.imprint","IMPRINT",EDGE,{"derivedFrom":sQuery(id+"F16.wireOp",EDGE,"E52.bottom")}),1.0]])]});
            var Q1;
            {var subQ0=sQuery(id+"F16.wireOp",EDGE,"E52.top");Q1=makeQuery(id+"F16.imprint","IMPRINT",FACE,{"disambiguationData":[TD([[makeQuery(id+"F16.imprint","IMPRINT",EDGE,{"derivedFrom":subQ0}),-1.0]])]});}
            var Q2;
            {var subQ0=sQuery(id+"F16.wireOp",EDGE,"E57");Q2=makeQuery(id+"F16.imprint","IMPRINT",FACE,{"disambiguationData":[TD([[makeQuery(id+"F16.imprint","IMPRINT",EDGE,{"derivedFrom":subQ0}),-1.0]])]});}
            extrude(context, id + "F17", {"entities" : qUnion([Q0, Q1, Q2]), "depth" : 7 * mm, "offsetDistance" : 25 * mm});
        }
        {
            var Q0;
            Q0=makeQuery(id+"F17.opExtrude","SWEPT_FACE",FACE,{"disambiguationData":[OSD([sQuery(id+"F16.wireOp",EDGE,"E56")])]});
            var Q1;
            Q1=makeQuery(id+"F17.opExtrude","SWEPT_FACE",FACE,{"disambiguationData":[OSD([sQuery(id+"F16.wireOp",EDGE,"E52.left")])]});
            var Q2;
            Q2=makeQuery(id+"F17.opExtrude","SWEPT_FACE",FACE,{"disambiguationData":[OSD([sQuery(id+"F16.wireOp",EDGE,"E53.2")])]});
            var Q3;
            Q3=makeQuery(id+"F17.opExtrude","SWEPT_FACE",FACE,{"disambiguationData":[OSD([sQuery(id+"F16.wireOp",EDGE,"E52.bottom")])]});
            var Q4;
            Q4=makeQuery(id+"F17.opExtrude","SWEPT_FACE",FACE,{"disambiguationData":[OSD([sQuery(id+"F16.wireOp",EDGE,"E52.top")])]});
            var Q5;
            Q5=makeQuery(id+"F17.opExtrude","SWEPT_FACE",FACE,{"disambiguationData":[OSD([sQuery(id+"F16.wireOp",EDGE,"E53.0")])]});
            var Q6;
            Q6=makeQuery(id+"F17.opExtrude","SWEPT_FACE",FACE,{"disambiguationData":[OSD([sQuery(id+"F16.wireOp",EDGE,"E53.1")])]});
            var Q7;
            Q7=makeQuery(id+"F17.opExtrude","SWEPT_BODY",BODY,{"disambiguationData":[OSD([sQuery(id+"F16.wireOp",EDGE,"E52.bottom"),sQuery(id+"F16.wireOp",EDGE,"E52.top"),sQuery(id+"F16.wireOp",EDGE,"E52.left"),sQuery(id+"F16.wireOp",EDGE,"E53.0"),sQuery(id+"F16.wireOp",EDGE,"E53.1"),sQuery(id+"F16.wireOp",EDGE,"E53.2"),sQuery(id+"F16.wireOp",EDGE,"E54"),sQuery(id+"F16.wireOp",EDGE,"E55"),sQuery(id+"F16.wireOp",EDGE,"E56"),sQuery(id+"F16.wireOp",EDGE,"E57")])]});
            shell(context, id + "F18", {"entities" : qUnion([Q0, Q1, Q2, Q3, Q4, Q5, Q6]), "parts" : qUnion([Q7]), "thickness" : 1 * mm});
        }
        {
            var Q0;
            Q0=makeQuery(id+"F16.imprint","IMPRINT",FACE,{"disambiguationData":[TD([[makeQuery(id+"F16.imprint","IMPRINT",EDGE,{"derivedFrom":sQuery(id+"F16.wireOp",EDGE,"E58.bottom")}),1.0]])]});
            var Q1;
            {var subQ0=sQuery(id+"F16.wireOp",EDGE,"E58.top");Q1=makeQuery(id+"F16.imprint","IMPRINT",FACE,{"disambiguationData":[TD([[makeQuery(id+"F16.imprint","IMPRINT",EDGE,{"derivedFrom":subQ0}),-1.0]])]});}
            var Q2;
            {var subQ0=sQuery(id+"F16.wireOp",EDGE,"E63");Q2=makeQuery(id+"F16.imprint","IMPRINT",FACE,{"disambiguationData":[TD([[makeQuery(id+"F16.imprint","IMPRINT",EDGE,{"derivedFrom":subQ0}),-1.0]])]});}
            var Q3;
            {var subQ9=sQuery(id+"F16.wireOp",EDGE,"E64.0");Q3=makeQuery(id+"F16.imprint","IMPRINT",FACE,{"disambiguationData":[TD([[makeQuery(id+"F16.imprint","IMPRINT",EDGE,{"derivedFrom":subQ9}),1.0]])]});}
            var Q4;
            {var subQ3=sQuery(id+"F16.wireOp",EDGE,"E66.0");Q4=makeQuery(id+"F16.imprint","IMPRINT",FACE,{"disambiguationData":[TD([[makeQuery(id+"F16.imprint","IMPRINT",EDGE,{"derivedFrom":subQ3}),-1.0]])]});}
            var Q5;
            {var subQ5=sQuery(id+"F16.wireOp",EDGE,"E65.0");Q5=makeQuery(id+"F16.imprint","IMPRINT",FACE,{"disambiguationData":[TD([[makeQuery(id+"F16.imprint","IMPRINT",EDGE,{"derivedFrom":subQ5}),-1.0]])]});}
            var Q6;
            {var subQ3=sQuery(id+"F16.wireOp",EDGE,"E61");Q6=makeQuery(id+"F16.imprint","IMPRINT",FACE,{"disambiguationData":[TD([[makeQuery(id+"F16.imprint","IMPRINT",EDGE,{"derivedFrom":subQ3}),-1.0]])]});}
            extrude(context, id + "F19", {"entities" : qUnion([Q0, Q1, Q2, Q3, Q4, Q5, Q6]), "depth" : 9 * mm, "offsetDistance" : 25 * mm});
        }
        {
            var Q0;
            {var subQ9=sQuery(id+"F16.wireOp",EDGE,"E64.0");Q0=makeQuery(id+"F16.imprint","IMPRINT",FACE,{"disambiguationData":[TD([[makeQuery(id+"F16.imprint","IMPRINT",EDGE,{"derivedFrom":subQ9}),1.0]])]});}
            var Q1;
            {var subQ3=sQuery(id+"F16.wireOp",EDGE,"E65.0");Q1=makeQuery(id+"F16.imprint","IMPRINT",FACE,{"disambiguationData":[TD([[makeQuery(id+"F16.imprint","IMPRINT",EDGE,{"derivedFrom":subQ3}),-1.0]])]});}
            var Q2;
            {var subQ3=sQuery(id+"F16.wireOp",EDGE,"E66.0");Q2=makeQuery(id+"F16.imprint","IMPRINT",FACE,{"disambiguationData":[TD([[makeQuery(id+"F16.imprint","IMPRINT",EDGE,{"derivedFrom":subQ3}),-1.0]])]});}
            extrude(context, id + "F20", {"entities" : qUnion([Q0, Q1, Q2]), "operationType" : NewBodyOperationType.REMOVE, "depth" : 7 * mm, "offsetDistance" : 25 * mm, "hasSecondDirection" : true, "secondDirectionOppositeDirection" : false, "secondDirectionDepth" : 2 * mm});
        }
        {
            var Q0;
            Q0=makeQuery(id+"F17.opExtrude","CAP_EDGE",EDGE,{"disambiguationData":[OSD([sQuery(id+"F16.wireOp",EDGE,"E57")])],"isStart":false});
            var Q1;
            Q1=makeQuery(id+"F17.opExtrude","CAP_EDGE",EDGE,{"disambiguationData":[OSD([sQuery(id+"F16.wireOp",EDGE,"E57")])],"isStart":true});
            var Q2;
            Q2=makeQuery(id+"F17.opExtrude","CAP_EDGE",EDGE,{"disambiguationData":[OSD([sQuery(id+"F16.wireOp",EDGE,"E55")])],"isStart":true});
            var Q3;
            Q3=makeQuery(id+"F17.opExtrude","CAP_EDGE",EDGE,{"disambiguationData":[OSD([sQuery(id+"F16.wireOp",EDGE,"E55")])],"isStart":false});
            var Q4;
            Q4=makeQuery(id+"F17.opExtrude","CAP_EDGE",EDGE,{"disambiguationData":[OSD([sQuery(id+"F16.wireOp",EDGE,"E54")])],"isStart":false});
            var Q5;
            Q5=makeQuery(id+"F17.opExtrude","CAP_EDGE",EDGE,{"disambiguationData":[OSD([sQuery(id+"F16.wireOp",EDGE,"E54")])],"isStart":true});
            var Q6;
            Q6=makeQuery(id+"F19.opExtrude","CAP_EDGE",EDGE,{"disambiguationData":[OSD([sQuery(id+"F16.wireOp",EDGE,"E63")])],"isStart":false});
            var Q7;
            Q7=makeQuery(id+"F19.opExtrude","CAP_EDGE",EDGE,{"disambiguationData":[OSD([sQuery(id+"F16.wireOp",EDGE,"E63")])],"isStart":true});
            var Q8;
            Q8=makeQuery(id+"F19.opExtrude","CAP_EDGE",EDGE,{"disambiguationData":[OSD([sQuery(id+"F16.wireOp",EDGE,"E61")])],"isStart":false});
            var Q9;
            Q9=makeQuery(id+"F19.opExtrude","CAP_EDGE",EDGE,{"disambiguationData":[OSD([sQuery(id+"F16.wireOp",EDGE,"E60")])],"isStart":false});
            var Q10;
            Q10=makeQuery(id+"F19.opExtrude","CAP_EDGE",EDGE,{"disambiguationData":[OSD([sQuery(id+"F16.wireOp",EDGE,"E60")])],"isStart":true});
            var Q11;
            Q11=makeQuery(id+"F19.opExtrude","CAP_EDGE",EDGE,{"disambiguationData":[OSD([sQuery(id+"F16.wireOp",EDGE,"E61")])],"isStart":true});
            fillet(context, id + "F21", {"entities" : qUnion([Q0, Q1, Q2, Q3, Q4, Q5, Q6, Q7, Q8, Q9, Q10, Q11]), "radius" : 3 * mm, "tangentPropagation" : true, "allowEdgeOverflow" : false});
        }
        {
            var Q0;
            {var subQ0=sQuery(id+"F16.wireOp",EDGE,"E57");Q0=makeQuery(id+"F18.opShell","OFFSET_EDGE",EDGE,{"disambiguationData":[OSD([subQ0]),TDD([makeQuery(id+"F17.opExtrude","CAP_EDGE",EDGE,{"disambiguationData":[OSD([subQ0])],"isStart":false})])]});}
            var Q1;
            {var subQ0=sQuery(id+"F16.wireOp",EDGE,"E57");Q1=makeQuery(id+"F18.opShell","OFFSET_EDGE",EDGE,{"disambiguationData":[OSD([subQ0]),TDD([makeQuery(id+"F17.opExtrude","CAP_EDGE",EDGE,{"disambiguationData":[OSD([subQ0])],"isStart":true})])]});}
            var Q2;
            {var subQ0=sQuery(id+"F16.wireOp",EDGE,"E55");Q2=makeQuery(id+"F18.opShell","OFFSET_EDGE",EDGE,{"disambiguationData":[OSD([subQ0]),TDD([makeQuery(id+"F17.opExtrude","CAP_EDGE",EDGE,{"disambiguationData":[OSD([subQ0])],"isStart":true})])]});}
            var Q3;
            {var subQ0=sQuery(id+"F16.wireOp",EDGE,"E54");Q3=makeQuery(id+"F18.opShell","OFFSET_EDGE",EDGE,{"disambiguationData":[OSD([subQ0]),TDD([makeQuery(id+"F17.opExtrude","CAP_EDGE",EDGE,{"disambiguationData":[OSD([subQ0])],"isStart":true})])]});}
            var Q4;
            {var subQ0=sQuery(id+"F16.wireOp",EDGE,"E55");Q4=makeQuery(id+"F18.opShell","OFFSET_EDGE",EDGE,{"disambiguationData":[OSD([subQ0]),TDD([makeQuery(id+"F17.opExtrude","CAP_EDGE",EDGE,{"disambiguationData":[OSD([subQ0])],"isStart":false})])]});}
            var Q5;
            {var subQ0=sQuery(id+"F16.wireOp",EDGE,"E54");Q5=makeQuery(id+"F18.opShell","OFFSET_EDGE",EDGE,{"disambiguationData":[OSD([subQ0]),TDD([makeQuery(id+"F17.opExtrude","CAP_EDGE",EDGE,{"disambiguationData":[OSD([subQ0])],"isStart":false})])]});}
            var Q6;
            Q6=makeQuery(id+"F17.opExtrude","SWEPT_EDGE",EDGE,{"disambiguationData":[OSD([sQuery(id+"F16.wireOp",EDGE,"E53.0"),sQuery(id+"F16.wireOp",EDGE,"E53.1")])]});
            var Q7;
            Q7=makeQuery(id+"F18.opShell","OFFSET_EDGE",EDGE,{"disambiguationData":[OSD([sQuery(id+"F16.wireOp",EDGE,"E53.0"),sQuery(id+"F16.wireOp",EDGE,"E53.1")])]});
            var Q8;
            Q8=makeQuery(id+"F17.opExtrude","SWEPT_EDGE",EDGE,{"disambiguationData":[OSD([sQuery(id+"F16.wireOp",EDGE,"E52.bottom"),sQuery(id+"F16.wireOp",EDGE,"E52.left")])]});
            var Q9;
            Q9=makeQuery(id+"F18.opShell","OFFSET_EDGE",EDGE,{"disambiguationData":[OSD([sQuery(id+"F16.wireOp",EDGE,"E52.bottom"),sQuery(id+"F16.wireOp",EDGE,"E52.left")])]});
            var Q10;
            Q10=makeQuery(id+"F18.opShell","OFFSET_EDGE",EDGE,{"disambiguationData":[OSD([sQuery(id+"F16.wireOp",EDGE,"E53.2"),sQuery(id+"F16.wireOp",EDGE,"E56")])]});
            var Q11;
            Q11=makeQuery(id+"F17.opExtrude","SWEPT_EDGE",EDGE,{"disambiguationData":[OSD([sQuery(id+"F16.wireOp",EDGE,"E53.2"),sQuery(id+"F16.wireOp",EDGE,"E56")])]});
            var Q12;
            Q12=makeQuery(id+"F18.opShell","OFFSET_EDGE",EDGE,{"disambiguationData":[OSD([sQuery(id+"F16.wireOp",EDGE,"E52.top"),sQuery(id+"F16.wireOp",EDGE,"E52.left"),sQuery(id+"F16.wireOp",EDGE,"E56")])]});
            var Q13;
            Q13=makeQuery(id+"F17.opExtrude","SWEPT_EDGE",EDGE,{"disambiguationData":[OSD([sQuery(id+"F16.wireOp",EDGE,"E52.top"),sQuery(id+"F16.wireOp",EDGE,"E52.left"),sQuery(id+"F16.wireOp",EDGE,"E56")])]});
            var Q14;
            Q14=makeQuery(id+"F20.boolean.opBoolean","COPY",EDGE,{"derivedFrom":makeQuery(id+"F20.opExtrude","CAP_EDGE",EDGE,{"disambiguationData":[OSD([sQuery(id+"F16.wireOp",EDGE,"E66.0")])],"isStart":true})});
            var Q15;
            Q15=makeQuery(id+"F20.boolean.opBoolean","COPY",EDGE,{"derivedFrom":makeQuery(id+"F20.opExtrude","CAP_EDGE",EDGE,{"disambiguationData":[OSD([sQuery(id+"F16.wireOp",EDGE,"E66.0")])],"isStart":false})});
            var Q16;
            {var subQ0=sQuery(id+"F16.wireOp",EDGE,"E62");var subQ1=sQuery(id+"F16.wireOp",EDGE,"E59.2");var subQ2=sQuery(id+"F16.wireOp",EDGE,"E59.1");var subQ3=sQuery(id+"F16.wireOp",EDGE,"E59.0");var subQ4=sQuery(id+"F16.wireOp",EDGE,"E58.left");var subQ5=sQuery(id+"F16.wireOp",EDGE,"E58.top");var subQ6=sQuery(id+"F16.wireOp",EDGE,"E58.bottom");Q16=makeQuery(id+"F20.boolean.opBoolean","SPLIT",EDGE,{"disambiguationData":[TD([makeQuery(id+"F19.opExtrude","CAP_FACE",FACE,{"disambiguationData":[OSD([subQ6,subQ5,subQ4,subQ3,subQ2,subQ1,sQuery(id+"F16.wireOp",EDGE,"E60"),sQuery(id+"F16.wireOp",EDGE,"E61"),subQ0,sQuery(id+"F16.wireOp",EDGE,"E63")])],"isStart":true})])],"derivedFrom":makeQuery(id+"F19.opExtrude","SWEPT_EDGE",EDGE,{"disambiguationData":[OSD([subQ3,subQ2])]})});}
            var Q17;
            {var subQ0=sQuery(id+"F16.wireOp",EDGE,"E62");var subQ1=sQuery(id+"F16.wireOp",EDGE,"E59.2");var subQ2=sQuery(id+"F16.wireOp",EDGE,"E59.1");var subQ3=sQuery(id+"F16.wireOp",EDGE,"E59.0");var subQ4=sQuery(id+"F16.wireOp",EDGE,"E58.left");var subQ5=sQuery(id+"F16.wireOp",EDGE,"E58.top");var subQ6=sQuery(id+"F16.wireOp",EDGE,"E58.bottom");Q17=makeQuery(id+"F20.boolean.opBoolean","SPLIT",EDGE,{"disambiguationData":[TD([makeQuery(id+"F19.opExtrude","CAP_FACE",FACE,{"disambiguationData":[OSD([subQ6,subQ5,subQ4,subQ3,subQ2,subQ1,sQuery(id+"F16.wireOp",EDGE,"E60"),sQuery(id+"F16.wireOp",EDGE,"E61"),subQ0,sQuery(id+"F16.wireOp",EDGE,"E63")])],"isStart":false})])],"derivedFrom":makeQuery(id+"F19.opExtrude","SWEPT_EDGE",EDGE,{"disambiguationData":[OSD([subQ3,subQ2])]})});}
            var Q18;
            Q18=makeQuery(id+"F20.boolean.opBoolean","COPY",EDGE,{"derivedFrom":makeQuery(id+"F20.opExtrude","CAP_EDGE",EDGE,{"disambiguationData":[OSD([sQuery(id+"F16.wireOp",EDGE,"E64.0")])],"isStart":true})});
            var Q19;
            Q19=makeQuery(id+"F20.boolean.opBoolean","COPY",EDGE,{"derivedFrom":makeQuery(id+"F20.opExtrude","CAP_EDGE",EDGE,{"disambiguationData":[OSD([sQuery(id+"F16.wireOp",EDGE,"E64.0")])],"isStart":false})});
            var Q20;
            Q20=makeQuery(id+"F20.boolean.opBoolean","COPY",EDGE,{"derivedFrom":makeQuery(id+"F20.opExtrude","CAP_EDGE",EDGE,{"disambiguationData":[OSD([sQuery(id+"F16.wireOp",EDGE,"E65.0")])],"isStart":true})});
            var Q21;
            Q21=makeQuery(id+"F20.boolean.opBoolean","COPY",EDGE,{"derivedFrom":makeQuery(id+"F20.opExtrude","CAP_EDGE",EDGE,{"disambiguationData":[OSD([sQuery(id+"F16.wireOp",EDGE,"E65.0")])],"isStart":false})});
            var Q22;
            {var subQ0=sQuery(id+"F16.wireOp",EDGE,"E62");var subQ1=sQuery(id+"F16.wireOp",EDGE,"E59.2");var subQ2=sQuery(id+"F16.wireOp",EDGE,"E59.1");var subQ3=sQuery(id+"F16.wireOp",EDGE,"E59.0");var subQ4=sQuery(id+"F16.wireOp",EDGE,"E58.left");var subQ5=sQuery(id+"F16.wireOp",EDGE,"E58.top");var subQ6=sQuery(id+"F16.wireOp",EDGE,"E58.bottom");Q22=makeQuery(id+"F20.boolean.opBoolean","SPLIT",EDGE,{"disambiguationData":[TD([makeQuery(id+"F19.opExtrude","CAP_FACE",FACE,{"disambiguationData":[OSD([subQ6,subQ5,subQ4,subQ3,subQ2,subQ1,sQuery(id+"F16.wireOp",EDGE,"E60"),sQuery(id+"F16.wireOp",EDGE,"E61"),subQ0,sQuery(id+"F16.wireOp",EDGE,"E63")])],"isStart":false})])],"derivedFrom":makeQuery(id+"F19.opExtrude","SWEPT_EDGE",EDGE,{"disambiguationData":[OSD([subQ1,subQ0])]})});}
            var Q23;
            {var subQ0=sQuery(id+"F16.wireOp",EDGE,"E62");var subQ1=sQuery(id+"F16.wireOp",EDGE,"E59.2");var subQ2=sQuery(id+"F16.wireOp",EDGE,"E59.1");var subQ3=sQuery(id+"F16.wireOp",EDGE,"E59.0");var subQ4=sQuery(id+"F16.wireOp",EDGE,"E58.left");var subQ5=sQuery(id+"F16.wireOp",EDGE,"E58.top");var subQ6=sQuery(id+"F16.wireOp",EDGE,"E58.bottom");Q23=makeQuery(id+"F20.boolean.opBoolean","SPLIT",EDGE,{"disambiguationData":[TD([makeQuery(id+"F19.opExtrude","CAP_FACE",FACE,{"disambiguationData":[OSD([subQ6,subQ5,subQ4,subQ3,subQ2,subQ1,sQuery(id+"F16.wireOp",EDGE,"E60"),sQuery(id+"F16.wireOp",EDGE,"E61"),subQ0,sQuery(id+"F16.wireOp",EDGE,"E63")])],"isStart":true})])],"derivedFrom":makeQuery(id+"F19.opExtrude","SWEPT_EDGE",EDGE,{"disambiguationData":[OSD([subQ1,subQ0])]})});}
            fillet(context, id + "F22", {"entities" : qUnion([Q0, Q1, Q2, Q3, Q4, Q5, Q6, Q7, Q8, Q9, Q10, Q11, Q12, Q13, Q14, Q15, Q16, Q17, Q18, Q19, Q20, Q21, Q22, Q23]), "radius" : 1 * mm, "tangentPropagation" : true, "allowEdgeOverflow" : false});
        }
        {
            var Q0;
            Q0=makeQuery(id+"F1.opExtrude","SWEPT_BODY",BODY,{"disambiguationData":[OSD([sQuery(id+"F0.wireOp",EDGE,"E0"),sQuery(id+"F0.wireOp",EDGE,"E1"),sQuery(id+"F0.wireOp",EDGE,"E2"),sQuery(id+"F0.wireOp",EDGE,"E3"),sQuery(id+"F0.wireOp",EDGE,"E4"),sQuery(id+"F0.wireOp",EDGE,"E5"),sQuery(id+"F0.wireOp",EDGE,"E6"),sQuery(id+"F0.wireOp",EDGE,"E7"),sQuery(id+"F0.wireOp",EDGE,"E9.trimOffspring"),sQuery(id+"F0.wireOp",EDGE,"E10"),sQuery(id+"F0.wireOp",EDGE,"E11"),sQuery(id+"F0.wireOp",EDGE,"E12.0"),sQuery(id+"F0.wireOp",EDGE,"E13"),sQuery(id+"F0.wireOp",EDGE,"E14"),sQuery(id+"F0.wireOp",EDGE,"E16.0")])]});
            var Q1;
            Q1=makeQuery(id+"F4.opExtrude","SWEPT_BODY",BODY,{"disambiguationData":[OSD([sQuery(id+"F0.wireOp",EDGE,"E0"),sQuery(id+"F0.wireOp",EDGE,"E1"),sQuery(id+"F0.wireOp",EDGE,"E2"),sQuery(id+"F0.wireOp",EDGE,"E3"),sQuery(id+"F0.wireOp",EDGE,"E4"),sQuery(id+"F0.wireOp",EDGE,"E5"),sQuery(id+"F0.wireOp",EDGE,"E6"),sQuery(id+"F0.wireOp",EDGE,"E7"),sQuery(id+"F0.wireOp",EDGE,"E9.trimOffspring"),sQuery(id+"F0.wireOp",EDGE,"E10"),sQuery(id+"F0.wireOp",EDGE,"E11"),sQuery(id+"F0.wireOp",EDGE,"E12.0"),sQuery(id+"F0.wireOp",EDGE,"E13"),sQuery(id+"F0.wireOp",EDGE,"E14"),sQuery(id+"F0.wireOp",EDGE,"E16.0")])]});
            var Q2;
            Q2=makeQuery(id+"F12.opExtrude","SWEPT_BODY",BODY,{"disambiguationData":[OSD([sQuery(id+"F7.wireOp",EDGE,"E19"),sQuery(id+"F7.wireOp",EDGE,"E20"),sQuery(id+"F7.wireOp",EDGE,"E21"),sQuery(id+"F7.wireOp",EDGE,"E22"),sQuery(id+"F7.wireOp",EDGE,"E23"),sQuery(id+"F7.wireOp",EDGE,"E24")])]});
            var Q3;
            Q3=makeQuery(id+"F17.opExtrude","SWEPT_BODY",BODY,{"disambiguationData":[OSD([sQuery(id+"F16.wireOp",EDGE,"E52.bottom"),sQuery(id+"F16.wireOp",EDGE,"E52.top"),sQuery(id+"F16.wireOp",EDGE,"E52.left"),sQuery(id+"F16.wireOp",EDGE,"E53.0"),sQuery(id+"F16.wireOp",EDGE,"E53.1"),sQuery(id+"F16.wireOp",EDGE,"E53.2"),sQuery(id+"F16.wireOp",EDGE,"E54"),sQuery(id+"F16.wireOp",EDGE,"E55"),sQuery(id+"F16.wireOp",EDGE,"E56"),sQuery(id+"F16.wireOp",EDGE,"E57")])]});
            deleteBodies(context, id + "F23", {"entities" : qUnion([Q0, Q1, Q2, Q3])});
        }
    });
